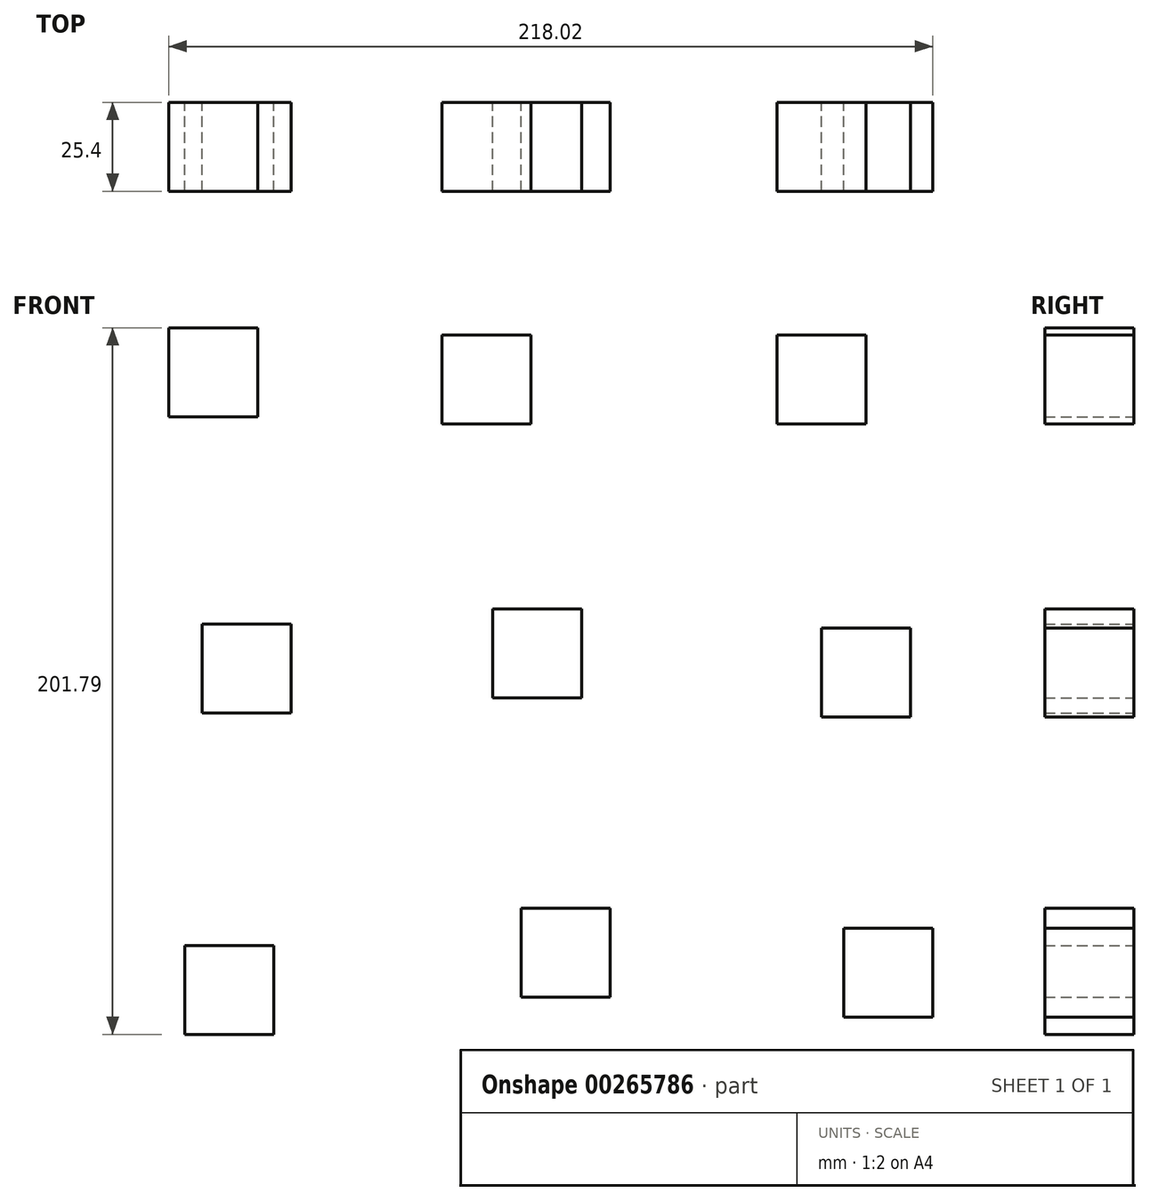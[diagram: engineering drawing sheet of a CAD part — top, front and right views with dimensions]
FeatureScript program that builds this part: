
annotation { "Feature Type Name" : "Feature", "Feature Type Description" : "" }
export const myFeature = defineFeature(function(context is Context, id is Id, definition is map)
    precondition{}
    {
        {
            var Q0;
            Q0=qCreatedBy(makeId("Front.planeOp"),FACE);
            var sketch = newSketch(context, id + "F0", { "sketchPlane" : qUnion([Q0])});
            skLineSegment(sketch, "E0.bottom", {"start": v(-107.7, 105.66) * mm, "end": v(-82.3, 105.66) * mm});
            skLineSegment(sketch, "E0.top", {"start": v(-107.7, 80.26) * mm, "end": v(-82.3, 80.26) * mm});
            skLineSegment(sketch, "E0.left", {"start": v(-107.7, 105.66) * mm, "end": v(-107.7, 80.26) * mm});
            skLineSegment(sketch, "E0.right", {"start": v(-82.3, 105.66) * mm, "end": v(-82.3, 80.26) * mm});
            skLineSegment(sketch, "E1.bottom", {"start": v(-29.74, 103.54) * mm, "end": v(-4.34, 103.54) * mm});
            skLineSegment(sketch, "E1.top", {"start": v(-29.74, 78.14) * mm, "end": v(-4.34, 78.14) * mm});
            skLineSegment(sketch, "E1.left", {"start": v(-29.74, 103.54) * mm, "end": v(-29.74, 78.14) * mm});
            skLineSegment(sketch, "E1.right", {"start": v(-4.34, 103.54) * mm, "end": v(-4.34, 78.14) * mm});
            skLineSegment(sketch, "E2.bottom", {"start": v(65.86, 103.54) * mm, "end": v(91.26, 103.54) * mm});
            skLineSegment(sketch, "E2.top", {"start": v(65.86, 78.14) * mm, "end": v(91.26, 78.14) * mm});
            skLineSegment(sketch, "E2.left", {"start": v(65.86, 103.54) * mm, "end": v(65.86, 78.14) * mm});
            skLineSegment(sketch, "E2.right", {"start": v(91.26, 103.54) * mm, "end": v(91.26, 78.14) * mm});
            skLineSegment(sketch, "E3.bottom", {"start": v(-98.18, 21) * mm, "end": v(-72.78, 21) * mm});
            skLineSegment(sketch, "E3.top", {"start": v(-98.18, -4.4) * mm, "end": v(-72.78, -4.4) * mm});
            skLineSegment(sketch, "E3.left", {"start": v(-98.18, 21) * mm, "end": v(-98.18, -4.4) * mm});
            skLineSegment(sketch, "E3.right", {"start": v(-72.78, 21) * mm, "end": v(-72.78, -4.4) * mm});
            skLineSegment(sketch, "E4.bottom", {"start": v(-15.28, 25.4) * mm, "end": v(10.12, 25.4) * mm});
            skLineSegment(sketch, "E4.top", {"start": v(-15.28, 0) * mm, "end": v(10.12, 0) * mm});
            skLineSegment(sketch, "E4.left", {"start": v(-15.28, 25.4) * mm, "end": v(-15.28, 0) * mm});
            skLineSegment(sketch, "E4.right", {"start": v(10.12, 25.4) * mm, "end": v(10.12, 0) * mm});
            skLineSegment(sketch, "E5.bottom", {"start": v(78.56, 19.93) * mm, "end": v(103.96, 19.93) * mm});
            skLineSegment(sketch, "E5.top", {"start": v(78.56, -5.47) * mm, "end": v(103.96, -5.47) * mm});
            skLineSegment(sketch, "E5.left", {"start": v(78.56, 19.93) * mm, "end": v(78.56, -5.47) * mm});
            skLineSegment(sketch, "E5.right", {"start": v(103.96, 19.93) * mm, "end": v(103.96, -5.47) * mm});
            skLineSegment(sketch, "E6.bottom", {"start": v(-103.12, -70.73) * mm, "end": v(-77.72, -70.73) * mm});
            skLineSegment(sketch, "E6.top", {"start": v(-103.12, -96.13) * mm, "end": v(-77.72, -96.13) * mm});
            skLineSegment(sketch, "E6.left", {"start": v(-103.12, -70.73) * mm, "end": v(-103.12, -96.13) * mm});
            skLineSegment(sketch, "E6.right", {"start": v(-77.72, -70.73) * mm, "end": v(-77.72, -96.13) * mm});
            skLineSegment(sketch, "E7.bottom", {"start": v(-7.16, -60.15) * mm, "end": v(18.24, -60.15) * mm});
            skLineSegment(sketch, "E7.top", {"start": v(-7.16, -85.55) * mm, "end": v(18.24, -85.55) * mm});
            skLineSegment(sketch, "E7.left", {"start": v(-7.16, -60.15) * mm, "end": v(-7.16, -85.55) * mm});
            skLineSegment(sketch, "E7.right", {"start": v(18.24, -60.15) * mm, "end": v(18.24, -85.55) * mm});
            skLineSegment(sketch, "E8.bottom", {"start": v(84.91, -65.8) * mm, "end": v(110.31, -65.8) * mm});
            skLineSegment(sketch, "E8.top", {"start": v(84.91, -91.2) * mm, "end": v(110.31, -91.2) * mm});
            skLineSegment(sketch, "E8.left", {"start": v(84.91, -65.8) * mm, "end": v(84.91, -91.2) * mm});
            skLineSegment(sketch, "E8.right", {"start": v(110.31, -65.8) * mm, "end": v(110.31, -91.2) * mm});
            skSolve(sketch);
        }
        {
            var Q0;
            Q0 = qSketchRegion(id + "F0", true);
            extrude(context, id + "F1", {"entities" : qUnion([Q0]), "depth" : 25.4 * mm});
        }
    });
